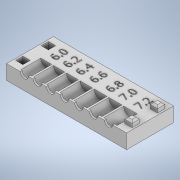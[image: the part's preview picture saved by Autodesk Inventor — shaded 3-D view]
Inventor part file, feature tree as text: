
AUTODESK INVENTOR PART (.ipt)
format: ipt  version: 2021 (Build 250183000, 183)  size: 723,456 bytes
history: native  units: mm
features: extrude x9, sketch x9, chamfer x1
ambient origin geometry x8: Origin, YZ Plane, XZ Plane, XY Plane, X Axis, Y Axis, Z Axis, Center Point
bodies: Solid1 (feature_tree)
feature tree (19):
  extrude  "Extrusion1"  Depth=56.0mm
  extrude  "Extrusion2"  Depth=8.0mm
  extrude  "Extrusion3"  Depth=6.4mm
  extrude  "Extrusion4"  Depth=7.0mm
  extrude  "Extrusion5"  Depth=4.85mm
  extrude  "Extrusion6"  Depth=1.0mm
  extrude  "Extrusion7"  Depth=1.0mm
  extrude  "Extrusion8"  Depth=1.0mm
  extrude  "Extrusion9"  Depth=11.0mm TaperAngle=0.0deg
  chamfer  "Chamfer1"  Distance=8.0mm
  sketch  "Sketch1"  dims[d0=15.0mm d1=56.0mm]
  sketch  "Sketch2"  dims[d2=8.0mm d3=0.0mm d4=6.0mm]
  sketch  "Sketch3"  dims[d5=6.2mm d6=6.4mm]
  sketch  "Sketch5"  dims[d7=6.8mm d8=7.0mm]
  sketch  "Sketch6"  dims[d9=7.2mm d10=4.85mm]
  sketch  "Sketch7"  dims[d12=1.0mm d13=1.0mm]
  sketch  "Sketch8"  dims[d14=1.0mm d15=1.0mm]
  sketch  "Sketch9"  dims[d17=1.0mm d18=7.4mm]
  sketch  "Sketch10"  dims[d19=1.0mm d20=11.0mm d21=0.0mm d22=8.0mm d23=0.0mm d25=3.0mm d26=10.0mm d27=14.0mm d28=14.0mm d29=17.0mm d30=14.0mm d31=14.0mm d32=24.5mm d34=14.0mm d35=14.0mm d36=0.5mm d37=0.0mm d38=1.0mm d39=0.0mm d40=4.5mm d41=4.5mm d42=4.5mm d43=4.5mm d44=4.5mm d45=4.5mm d46=4.5mm d47=100.0mm d48=0.0mm d49=5.0mm d50=0.0mm d51=5.0mm d52=8.0mm d53=0.0mm d54=4.0mm d55=4.0mm d56=4.0mm d57=4.0mm d58=4.0mm d59=4.0mm d60=4.0mm d61=4.0mm d62=1.0mm d63=10.0mm d64=4.0mm d65=10.0mm d68=1.0mm d69=0.0mm d70=3.0mm d71=0.0mm d72=1.0mm d73=1.0mm d74=4.0mm d75=4.0mm d76=4.0mm d77=4.0mm d78=4.0mm d79=10.0mm d80=5.0mm d81=0.0mm d82=1.0mm d83=2.0mm d84=45.0deg]
